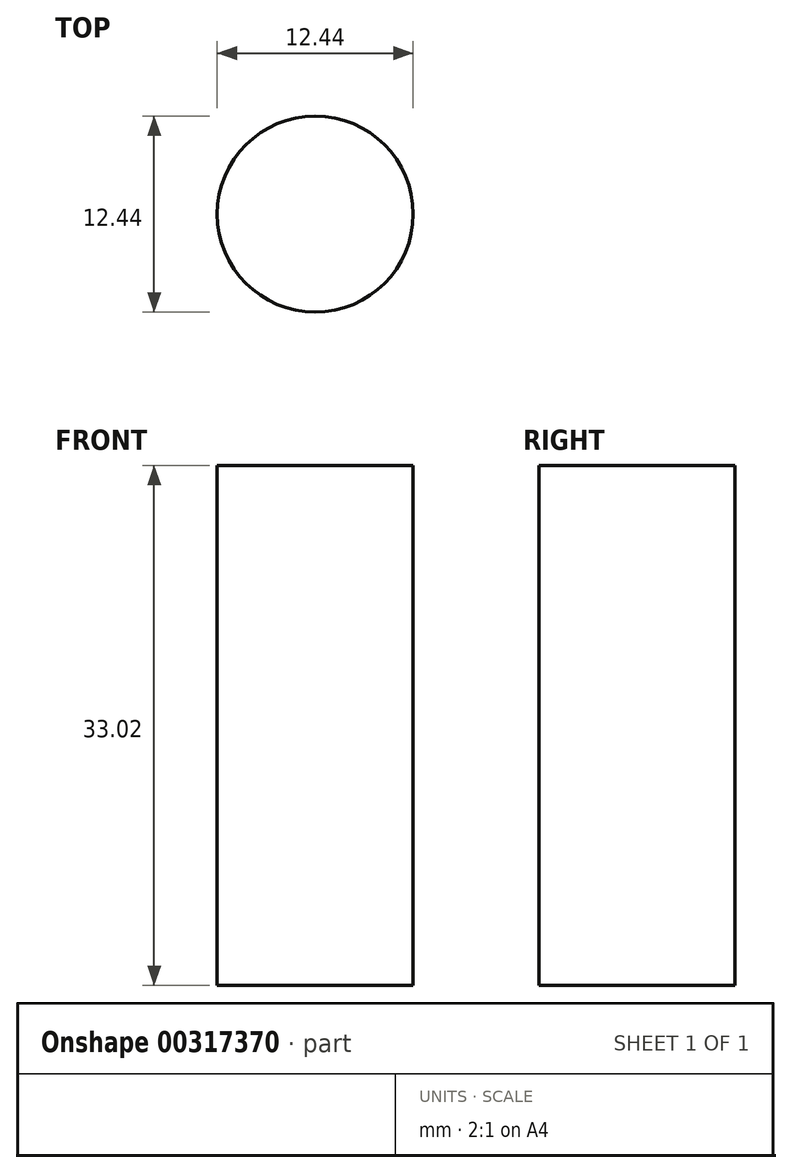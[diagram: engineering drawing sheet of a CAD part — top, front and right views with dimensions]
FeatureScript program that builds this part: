
annotation { "Feature Type Name" : "Feature", "Feature Type Description" : "" }
export const myFeature = defineFeature(function(context is Context, id is Id, definition is map)
    precondition{}
    {
        {
            var Q0;
            Q0=qCreatedBy(makeId("Top.planeOp"),FACE);
            var sketch = newSketch(context, id + "F0", { "sketchPlane" : qUnion([Q0])});
            skCircle(sketch, "E0", {"center": v(0, 0) * mm, "radius": 6.22 * mm});
            skSolve(sketch);
        }
        {
            var Q0;
            Q0=makeQuery(id+"F0.imprint","IMPRINT",FACE,{"disambiguationData":[TD([[makeQuery(id+"F0.imprint","IMPRINT",EDGE,{"derivedFrom":sQuery(id+"F0.wireOp",EDGE,"E0")}),1.0]])]});
            extrude(context, id + "F1", {"entities" : qUnion([Q0]), "depth" : 33.02 * mm});
        }
    });
